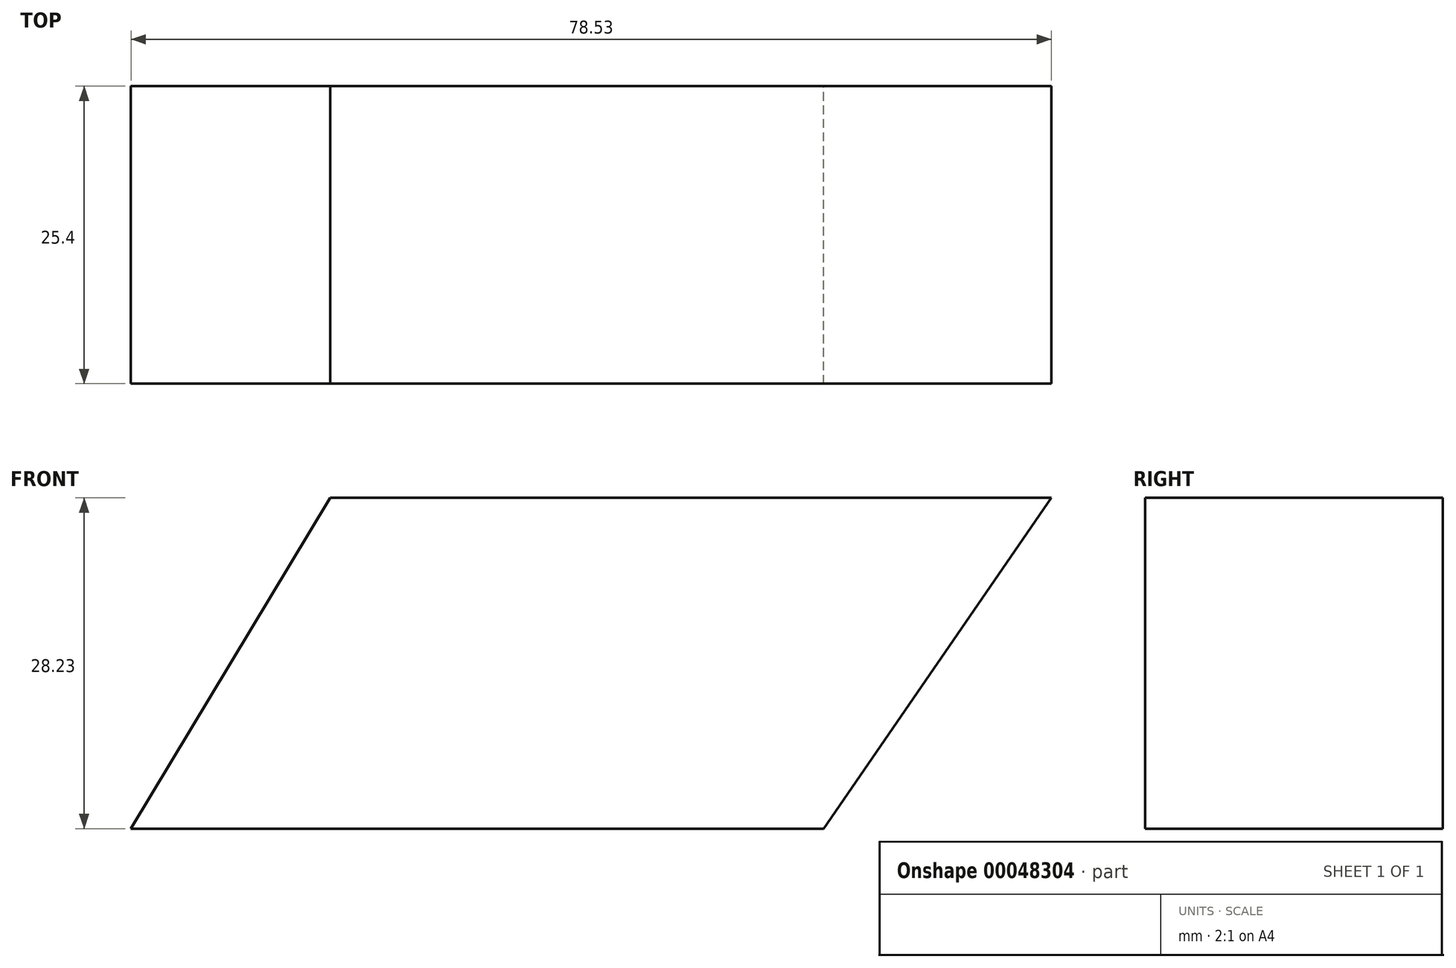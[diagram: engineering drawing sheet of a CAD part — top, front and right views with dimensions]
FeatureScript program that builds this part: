
annotation { "Feature Type Name" : "Feature", "Feature Type Description" : "" }
export const myFeature = defineFeature(function(context is Context, id is Id, definition is map)
    precondition{}
    {
        {
            var Q0;
            Q0=qCreatedBy(makeId("Front.planeOp"),FACE);
            var sketch = newSketch(context, id + "F0", { "sketchPlane" : qUnion([Q0])});
            skLineSegment(sketch, "E0", {"start": v(-38.27, -0.49) * mm, "end": v(23.26, -0.49) * mm});
            skLineSegment(sketch, "E1", {"start": v(23.26, -0.49) * mm, "end": v(3.83, -28.72) * mm});
            skLineSegment(sketch, "E2", {"start": v(3.83, -28.72) * mm, "end": v(-55.27, -28.72) * mm});
            skLineSegment(sketch, "E3", {"start": v(-55.27, -28.72) * mm, "end": v(-38.27, -0.49) * mm});
            skSolve(sketch);
        }
        {
            var Q0;
            Q0 = qSketchRegion(id + "F0", true);
            extrude(context, id + "F1", {"entities" : qUnion([Q0]), "depth" : 25.4 * mm});
        }
    });
